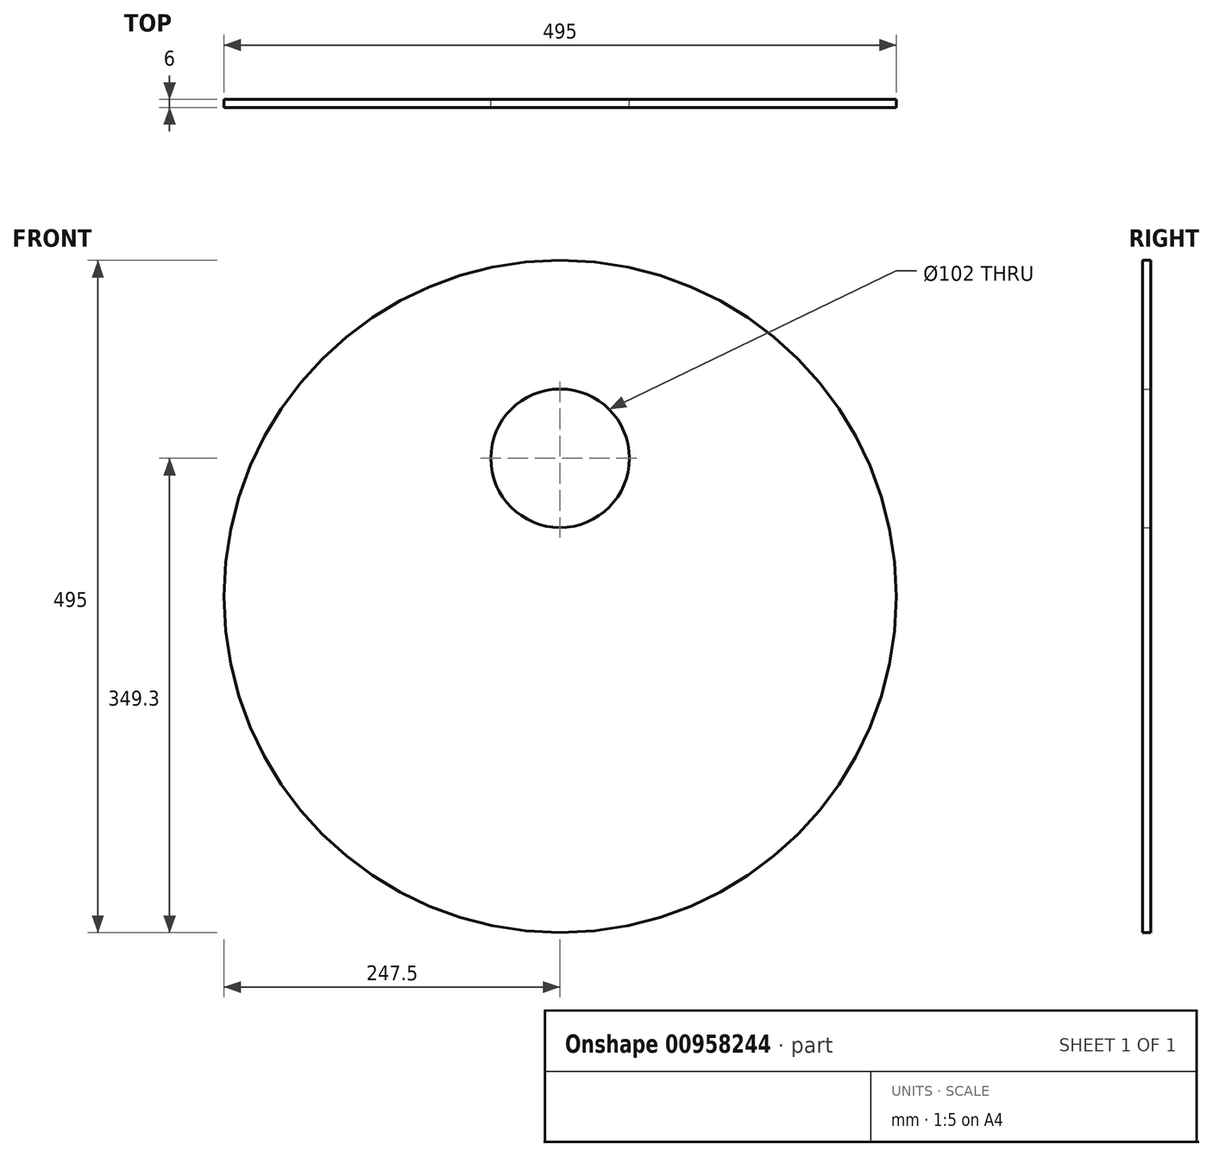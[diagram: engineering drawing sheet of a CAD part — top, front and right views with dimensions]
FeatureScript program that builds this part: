
annotation { "Feature Type Name" : "Feature", "Feature Type Description" : "" }
export const myFeature = defineFeature(function(context is Context, id is Id, definition is map)
    precondition{}
    {
        {
            var Q0;
            Q0=qCreatedBy(makeId("Front.planeOp"),FACE);
            var sketch = newSketch(context, id + "F0", { "sketchPlane" : qUnion([Q0])});
            skCircle(sketch, "E0", {"center": v(0, 0) * mm, "radius": 247.5 * mm});
            skCircle(sketch, "E1", {"center": v(0, 101.8) * mm, "radius": 51 * mm});
            skSolve(sketch);
        }
        {
            var Q0;
            Q0=makeQuery(id+"F0.imprint","IMPRINT",FACE,{"disambiguationData":[TD([[makeQuery(id+"F0.imprint","IMPRINT",EDGE,{"derivedFrom":sQuery(id+"F0.wireOp",EDGE,"E0")}),1.0]])]});
            extrude(context, id + "F1", {"entities" : qUnion([Q0]), "depth" : 6 * mm, "offsetDistance" : 25.4 * mm});
        }
    });
